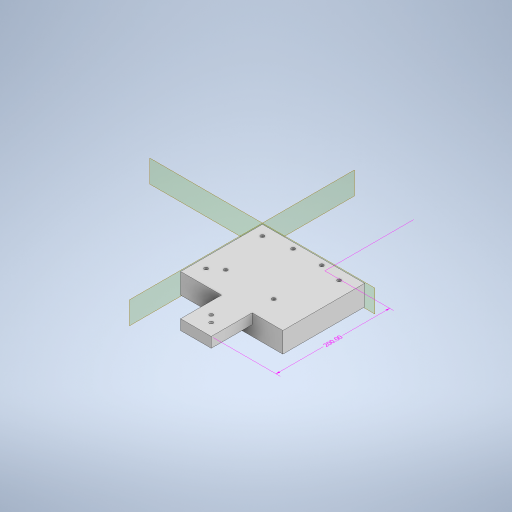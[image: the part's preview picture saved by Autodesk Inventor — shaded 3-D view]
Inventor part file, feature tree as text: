
AUTODESK INVENTOR PART (.ipt)
format: ipt  version: 2023 (Build 270158000, 158)  size: 432,128 bytes
history: native  units: mm
features: sketch x10, extrude x5, hole x5, other x3, plane x2, split x2
ambient origin geometry x8: Origin, YZ Plane, XZ Plane, XY Plane, X Axis, Y Axis, Z Axis, Center Point
bodies: Body1 (feature_tree)
feature tree (27):
  other  "Sólido1"
  other  "Anotaciones"
  extrude  "Extrusión1"  Depth=160.0mm
  extrude  "Extrusión2"  Depth=30.0mm
  hole  "Agujero1"  [1 undecoded]
  extrude  "Extrusión3"  Depth=11.75mm
  hole  "Agujero2"  [1 undecoded]
  hole  "Agujero3"  [1 undecoded]
  extrude  "Extrusión4"  TaperAngle=0.0deg  [1 undecoded]
  plane  "Plano de trabajo1"
  plane  "Plano de trabajo2"
  hole  "Agujero4"  [1 undecoded]
  hole  "Agujero5"  [1 undecoded]
  extrude  "Extrusión5"  Depth=70.0mm
  split  "Dividir1"
  split  "Dividir2"
  sketch  "Boceto1"  dims[d0=200.0mm d1=160.0mm]
  sketch  "Boceto2"  dims[d2=20.0mm d3=0.0mm d4=30.0mm]
  sketch  "Boceto3"  dims[d5=40.0mm d6=10.0mm d7=0.0mm]
  sketch  "Boceto4"  dims[d23=21.75mm d24=11.75mm]
  sketch  "Boceto5"  dims[d26=11.75mm]
  sketch  "Boceto6"  dims[d27=3.5mm d28=6.0mm d29=4.0mm d30=2.0mm d31=90.0deg d32=8.0mm d33=20.594885mm d34=30.0mm]
  sketch  "Boceto7"  dims[d35=10.0mm d36=30.0mm]
  sketch  "Boceto8"  dims[d37=40.0mm d38=0.0mm]
  sketch  "Boceto9"  dims[d39=10.0mm d40=10.0mm d41=40.0mm d42=0.0mm d43=6.5mm d44=6.5mm d45=3.5mm d46=3.5mm d47=11.749873mm d48=11.75mm d49=0.0mm]
  sketch  "Boceto10"  dims[d50=11.75mm d51=0.0mm d52=3.5mm d53=6.0mm d54=4.0mm d55=2.0mm d56=90.0deg d57=8.0mm d58=20.594885mm d59=7.0mm d60=7.0mm d61=7.0mm d62=39.0mm d63=46.0mm d64=59.0mm d65=46.0mm d66=39.0mm d67=59.0mm d68=52.0mm d69=70.0mm d70=22.0mm d71=42.0mm d72=3.5mm d73=3.5mm d74=3.5mm d75=3.5mm d76=3.5mm d77=6.0mm d78=4.0mm d79=2.0mm d80=90.0deg d81=8.0mm d82=20.594885mm d83=7.0mm d84=7.0mm d85=7.0mm d86=39.0mm d87=46.0mm d88=59.0mm d89=46.0mm d90=39.0mm d91=59.0mm d92=20.0mm d93=0.0mm d97=40.000127mm d98=10.0mm d99=30.0mm d100=10.0mm d101=5.0mm d102=5.0mm d103=5.0mm d104=5.0mm d105=45.0deg d106=45.0deg d107=10.0mm d108=10.0mm d109=30.0mm d110=5.0mm d111=5.0mm d112=5.0mm d113=5.0mm d114=10.0mm d115=30.0mm d116=5.0mm d117=5.0mm d118=5.0mm d119=5.0mm d120=10.0mm d121=3.5mm d122=6.0mm d123=4.0mm d124=2.0mm d125=90.0deg d126=8.0mm d127=20.594885mm d128=3.5mm d129=10.0mm d130=10.0mm d131=3.5mm d132=6.0mm d133=4.0mm d134=2.0mm d135=90.0deg d136=8.0mm d137=20.594885mm d138=32.0mm d139=32.0mm d140=10.0mm d141=0.0mm d142=17.37633mm d143=12.709242mm d144=6.683722mm d145=12.708891mm d146=5.220756mm d147=1.603663mm d148=2.153068mm d149=6.490327mm d94=6.100674mm d95=2.550465mm d96=200.0mm]
  other  "Cota lineal 1"
note: 6 required parameter values undecoded (feature->parameter linkage not recoverable at this tier; creation-order binding heuristic only, values carry confidence <= 0.55)
